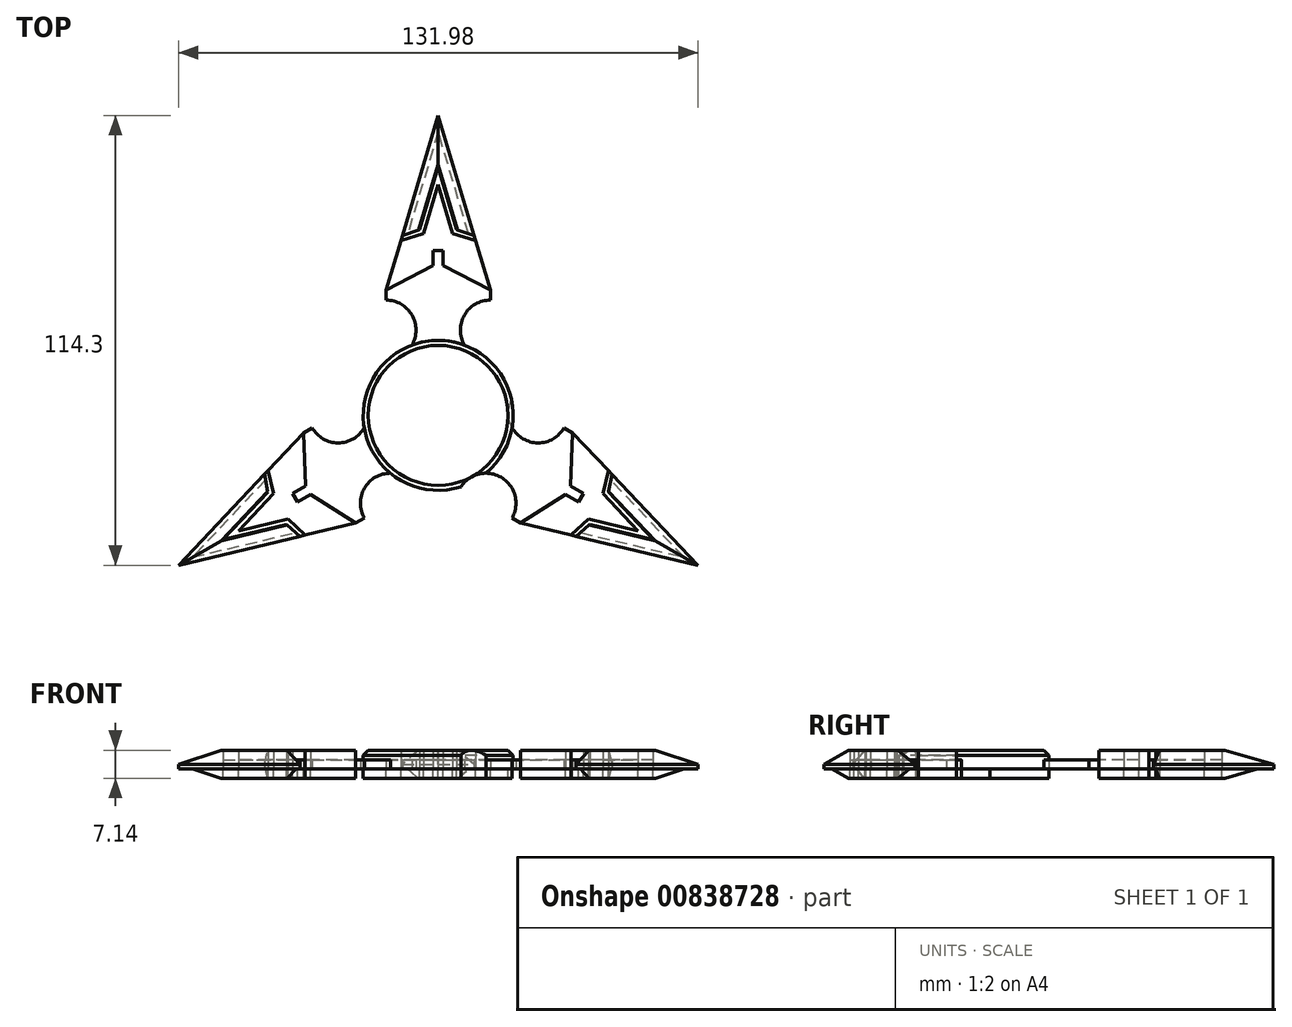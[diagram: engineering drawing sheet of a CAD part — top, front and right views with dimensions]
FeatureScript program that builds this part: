
annotation { "Feature Type Name" : "Feature", "Feature Type Description" : "" }
export const myFeature = defineFeature(function(context is Context, id is Id, definition is map)
    precondition{}
    {
        {
            var Q0;
            Q0=qCreatedBy(makeId("Top.planeOp"),FACE);
            var sketch = newSketch(context, id + "F0", { "sketchPlane" : qUnion([Q0])});
            skCircle(sketch, "E0", {"center": v(0, 0) * mm, "radius": 19.05 * mm});
            skLineSegment(sketch, "E1", {"start": v(0, 76.2) * mm, "end": v(-13.25, 31.83) * mm});
            skLineSegment(sketch, "E2", {"start": v(13.25, 31.83) * mm, "end": v(0, 76.2) * mm});
            skLineSegment(sketch, "E3", {"start": v(-13.25, 31.83) * mm, "end": v(-13.25, 29.3) * mm});
            skLineSegment(sketch, "E4", {"start": v(13.25, 31.83) * mm, "end": v(13.25, 29.3) * mm});
            skLineSegment(sketch, "E5", {"start": v(0, 0) * mm, "end": v(-4, 18.62) * mm});
            skPoint(sketch, "E6", {"position": v(-12.85, 14.06) * mm});
            skPoint(sketch, "E7", {"position": v(12.85, 14.06) * mm});
            skArc(sketch, "E8", {"start": v(-12.85, 14.06) * mm, "mid": v(-5.63, 21.87) * mm, "end": v(-13.25, 29.3) * mm});
            skArc(sketch, "E9", {"start": v(13.25, 29.3) * mm, "mid": v(5.63, 21.87) * mm, "end": v(12.85, 14.06) * mm});
            skPoint(sketch, "E10", {"position": v(0, 63.05) * mm});
            skPoint(sketch, "E11", {"position": v(-4.73, 47.22) * mm});
            skPoint(sketch, "E12", {"position": v(4.73, 47.22) * mm});
            skPoint(sketch, "E13", {"position": v(-9.1, 45.72) * mm});
            skPoint(sketch, "E14", {"position": v(9.12, 45.67) * mm});
            skLineSegment(sketch, "E15", {"start": v(-9.1, 45.72) * mm, "end": v(-4.73, 47.22) * mm});
            skLineSegment(sketch, "E16", {"start": v(0, 63.05) * mm, "end": v(-4.73, 47.22) * mm});
            skLineSegment(sketch, "E17", {"start": v(0, 63.05) * mm, "end": v(4.73, 47.22) * mm});
            skLineSegment(sketch, "E18", {"start": v(4.73, 47.22) * mm, "end": v(9.12, 45.67) * mm});
            skPoint(sketch, "E19", {"position": v(-9.48, 44.45) * mm});
            skPoint(sketch, "E20", {"position": v(9.48, 44.45) * mm});
            skPoint(sketch, "E21", {"position": v(0, 58.62) * mm});
            skLineSegment(sketch, "E22", {"start": v(-13.25, 31.83) * mm, "end": v(-1.27, 38.1) * mm});
            skLineSegment(sketch, "E23", {"start": v(-1.27, 38.1) * mm, "end": v(-1.27, 41.91) * mm});
            skLineSegment(sketch, "E24", {"start": v(-1.27, 41.91) * mm, "end": v(1.27, 41.91) * mm});
            skLineSegment(sketch, "E25", {"start": v(1.27, 41.91) * mm, "end": v(1.27, 38.1) * mm});
            skLineSegment(sketch, "E26", {"start": v(1.27, 38.1) * mm, "end": v(13.25, 31.83) * mm});
            skLineSegment(sketch, "E27", {"start": v(-9.48, 44.45) * mm, "end": v(-3.7, 46.2) * mm});
            skLineSegment(sketch, "E28", {"start": v(-3.7, 46.2) * mm, "end": v(0, 58.62) * mm});
            skLineSegment(sketch, "E29", {"start": v(0, 58.62) * mm, "end": v(3.7, 46.2) * mm});
            skLineSegment(sketch, "E30", {"start": v(3.7, 46.2) * mm, "end": v(9.48, 44.45) * mm});
            skPoint(sketch, "E31.1.0", {"position": v(-43.23, -14.01) * mm});
            skLineSegment(sketch, "E31.1.1", {"start": v(-66, -38.1) * mm, "end": v(-20.94, -27.39) * mm});
            skLineSegment(sketch, "E31.1.2", {"start": v(-33.63, -17.95) * mm, "end": v(-34.2, -4.44) * mm});
            skPoint(sketch, "E31.1.3", {"position": v(-54.6, -31.53) * mm});
            skLineSegment(sketch, "E31.1.4", {"start": v(-20.94, -27.39) * mm, "end": v(-32.36, -20.15) * mm});
            skLineSegment(sketch, "E31.1.5", {"start": v(-34.2, -4.44) * mm, "end": v(-66, -38.1) * mm});
            skPoint(sketch, "E31.1.6", {"position": v(-33.75, -30.44) * mm});
            skLineSegment(sketch, "E31.1.7", {"start": v(-54.6, -31.53) * mm, "end": v(-38.52, -27.7) * mm});
            skPoint(sketch, "E31.1.8", {"position": v(-38.52, -27.7) * mm});
            skLineSegment(sketch, "E31.1.9", {"start": v(-50.76, -29.3) * mm, "end": v(-41.86, -19.89) * mm});
            skPoint(sketch, "E31.1.10", {"position": v(-44.1, -14.94) * mm});
            skLineSegment(sketch, "E31.1.11", {"start": v(-54.6, -31.53) * mm, "end": v(-43.25, -19.51) * mm});
            skPoint(sketch, "E31.1.12", {"position": v(-50.76, -29.3) * mm});
            skPoint(sketch, "E31.1.13", {"position": v(-43.25, -19.51) * mm});
            skPoint(sketch, "E31.1.14", {"position": v(-35.04, -30.74) * mm});
            skLineSegment(sketch, "E31.1.15", {"start": v(-38.15, -26.3) * mm, "end": v(-50.76, -29.3) * mm});
            skLineSegment(sketch, "E31.1.16", {"start": v(-41.86, -19.89) * mm, "end": v(-43.23, -14.01) * mm});
            skLineSegment(sketch, "E31.1.17", {"start": v(-36.93, -19.86) * mm, "end": v(-33.63, -17.95) * mm});
            skLineSegment(sketch, "E31.1.18", {"start": v(-43.25, -19.51) * mm, "end": v(-44.1, -14.94) * mm});
            skLineSegment(sketch, "E31.1.19", {"start": v(-33.75, -30.44) * mm, "end": v(-38.15, -26.3) * mm});
            skLineSegment(sketch, "E31.1.20", {"start": v(-35.04, -30.74) * mm, "end": v(-38.52, -27.7) * mm});
            skLineSegment(sketch, "E31.1.21", {"start": v(-35.66, -22.05) * mm, "end": v(-36.93, -19.86) * mm});
            skLineSegment(sketch, "E31.1.22", {"start": v(-32.36, -20.15) * mm, "end": v(-35.66, -22.05) * mm});
            skLineSegment(sketch, "E31.1.23", {"start": v(-34.2, -4.44) * mm, "end": v(-32, -3.17) * mm});
            skLineSegment(sketch, "E31.1.24", {"start": v(-20.94, -27.39) * mm, "end": v(-18.74, -26.12) * mm});
            skArc(sketch, "E31.1.25", {"start": v(-32, -3.17) * mm, "mid": v(-21.75, -6.06) * mm, "end": v(-18.6, 4.1) * mm});
            skArc(sketch, "E31.1.26", {"start": v(-5.75, -18.16) * mm, "mid": v(-16.12, -15.81) * mm, "end": v(-18.74, -26.12) * mm});
            skPoint(sketch, "E31.2.0", {"position": v(33.75, -30.44) * mm});
            skLineSegment(sketch, "E31.2.1", {"start": v(66, -38.1) * mm, "end": v(34.2, -4.44) * mm});
            skLineSegment(sketch, "E31.2.2", {"start": v(32.36, -20.15) * mm, "end": v(20.94, -27.39) * mm});
            skPoint(sketch, "E31.2.3", {"position": v(54.6, -31.53) * mm});
            skLineSegment(sketch, "E31.2.4", {"start": v(34.2, -4.44) * mm, "end": v(33.63, -17.95) * mm});
            skLineSegment(sketch, "E31.2.5", {"start": v(20.94, -27.39) * mm, "end": v(66, -38.1) * mm});
            skPoint(sketch, "E31.2.6", {"position": v(43.23, -14.01) * mm});
            skLineSegment(sketch, "E31.2.7", {"start": v(54.6, -31.53) * mm, "end": v(43.25, -19.51) * mm});
            skPoint(sketch, "E31.2.8", {"position": v(43.25, -19.51) * mm});
            skLineSegment(sketch, "E31.2.9", {"start": v(50.76, -29.3) * mm, "end": v(38.15, -26.3) * mm});
            skPoint(sketch, "E31.2.10", {"position": v(35, -30.73) * mm});
            skLineSegment(sketch, "E31.2.11", {"start": v(54.6, -31.53) * mm, "end": v(38.52, -27.7) * mm});
            skPoint(sketch, "E31.2.12", {"position": v(50.76, -29.3) * mm});
            skPoint(sketch, "E31.2.13", {"position": v(38.52, -27.7) * mm});
            skPoint(sketch, "E31.2.14", {"position": v(44.15, -14.98) * mm});
            skLineSegment(sketch, "E31.2.15", {"start": v(41.86, -19.89) * mm, "end": v(50.76, -29.3) * mm});
            skLineSegment(sketch, "E31.2.16", {"start": v(38.15, -26.3) * mm, "end": v(33.75, -30.44) * mm});
            skLineSegment(sketch, "E31.2.17", {"start": v(35.66, -22.05) * mm, "end": v(32.36, -20.15) * mm});
            skLineSegment(sketch, "E31.2.18", {"start": v(38.52, -27.7) * mm, "end": v(35, -30.73) * mm});
            skLineSegment(sketch, "E31.2.19", {"start": v(43.23, -14.01) * mm, "end": v(41.86, -19.89) * mm});
            skLineSegment(sketch, "E31.2.20", {"start": v(44.15, -14.98) * mm, "end": v(43.25, -19.51) * mm});
            skLineSegment(sketch, "E31.2.21", {"start": v(36.93, -19.86) * mm, "end": v(35.66, -22.05) * mm});
            skLineSegment(sketch, "E31.2.22", {"start": v(33.63, -17.95) * mm, "end": v(36.93, -19.86) * mm});
            skLineSegment(sketch, "E31.2.23", {"start": v(20.94, -27.39) * mm, "end": v(18.74, -26.12) * mm});
            skLineSegment(sketch, "E31.2.24", {"start": v(34.2, -4.44) * mm, "end": v(32, -3.17) * mm});
            skArc(sketch, "E31.2.25", {"start": v(18.74, -26.12) * mm, "mid": v(16.12, -15.81) * mm, "end": v(5.75, -18.16) * mm});
            skArc(sketch, "E31.2.26", {"start": v(18.6, 4.1) * mm, "mid": v(21.75, -6.06) * mm, "end": v(32, -3.17) * mm});
            skArc(sketch, "E32", {"start": v(216.55, -0.25) * mm, "mid": v(245.18, 23.96) * mm, "end": v(209.9, 11.27) * mm});
            skLineSegment(sketch, "E33", {"start": v(228.68, 90.63) * mm, "end": v(219.2, 58.88) * mm});
            skLineSegment(sketch, "E34", {"start": v(241.93, 46.27) * mm, "end": v(228.68, 90.63) * mm});
            skLineSegment(sketch, "E35", {"start": v(241.93, 46.27) * mm, "end": v(241.93, 43.73) * mm});
            skPoint(sketch, "E36", {"position": v(215.83, 28.5) * mm});
            skPoint(sketch, "E37", {"position": v(241.53, 28.5) * mm});
            skArc(sketch, "E38", {"start": v(215.83, 28.5) * mm, "mid": v(223.05, 36.3) * mm, "end": v(215.43, 43.73) * mm});
            skArc(sketch, "E39", {"start": v(241.93, 43.73) * mm, "mid": v(234.3, 36.3) * mm, "end": v(241.53, 28.5) * mm});
            skPoint(sketch, "E40", {"position": v(228.68, 77.49) * mm});
            skPoint(sketch, "E41", {"position": v(223.95, 61.65) * mm});
            skPoint(sketch, "E42", {"position": v(233.4, 61.65) * mm});
            skPoint(sketch, "E43", {"position": v(219.58, 60.15) * mm});
            skPoint(sketch, "E44", {"position": v(237.8, 60.1) * mm});
            skLineSegment(sketch, "E45", {"start": v(219.58, 60.15) * mm, "end": v(223.95, 61.65) * mm});
            skLineSegment(sketch, "E46", {"start": v(228.68, 77.49) * mm, "end": v(223.95, 61.65) * mm});
            skLineSegment(sketch, "E47", {"start": v(228.68, 77.49) * mm, "end": v(233.4, 61.65) * mm});
            skLineSegment(sketch, "E48", {"start": v(233.4, 61.65) * mm, "end": v(237.8, 60.1) * mm});
            skPoint(sketch, "E49", {"position": v(219.2, 58.88) * mm});
            skPoint(sketch, "E50", {"position": v(238.16, 58.88) * mm});
            skPoint(sketch, "E51", {"position": v(228.68, 73.05) * mm});
            skLineSegment(sketch, "E52", {"start": v(215.43, 46.27) * mm, "end": v(227.4, 52.53) * mm});
            skLineSegment(sketch, "E53", {"start": v(227.4, 52.53) * mm, "end": v(227.4, 56.34) * mm});
            skLineSegment(sketch, "E54", {"start": v(227.4, 56.34) * mm, "end": v(229.95, 56.34) * mm});
            skLineSegment(sketch, "E55", {"start": v(229.95, 56.34) * mm, "end": v(229.95, 52.53) * mm});
            skLineSegment(sketch, "E56", {"start": v(229.95, 52.53) * mm, "end": v(241.93, 46.27) * mm});
            skLineSegment(sketch, "E57", {"start": v(219.2, 58.88) * mm, "end": v(224.97, 60.63) * mm});
            skLineSegment(sketch, "E58", {"start": v(224.97, 60.63) * mm, "end": v(228.68, 73.05) * mm});
            skLineSegment(sketch, "E59", {"start": v(228.68, 73.05) * mm, "end": v(232.39, 60.63) * mm});
            skLineSegment(sketch, "E60", {"start": v(232.39, 60.63) * mm, "end": v(238.16, 58.88) * mm});
            skPoint(sketch, "E61.1.0", {"position": v(185.44, 0.42) * mm});
            skLineSegment(sketch, "E61.1.1", {"start": v(193.63, -16.3) * mm, "end": v(194.92, -16) * mm});
            skLineSegment(sketch, "E61.1.2", {"start": v(195.05, -3.52) * mm, "end": v(194.49, 10) * mm});
            skPoint(sketch, "E61.1.3", {"position": v(174.07, -17.1) * mm});
            skLineSegment(sketch, "E61.1.4", {"start": v(207.73, -12.95) * mm, "end": v(196.32, -5.72) * mm});
            skLineSegment(sketch, "E61.1.5", {"start": v(194.49, 10) * mm, "end": v(185.44, 0.42) * mm});
            skPoint(sketch, "E61.1.6", {"position": v(194.92, -16) * mm});
            skPoint(sketch, "E61.1.8", {"position": v(190.15, -13.27) * mm});
            skPoint(sketch, "E61.1.10", {"position": v(184.57, -0.5) * mm});
            skPoint(sketch, "E61.1.12", {"position": v(177.92, -14.87) * mm});
            skPoint(sketch, "E61.1.13", {"position": v(185.42, -5.08) * mm});
            skPoint(sketch, "E61.1.14", {"position": v(193.63, -16.3) * mm});
            skLineSegment(sketch, "E61.1.17", {"start": v(191.75, -5.42) * mm, "end": v(195.05, -3.52) * mm});
            skLineSegment(sketch, "E61.1.21", {"start": v(193.02, -7.62) * mm, "end": v(191.75, -5.42) * mm});
            skLineSegment(sketch, "E61.1.22", {"start": v(196.32, -5.72) * mm, "end": v(193.02, -7.62) * mm});
            skLineSegment(sketch, "E61.1.23", {"start": v(194.49, 10) * mm, "end": v(196.69, 11.26) * mm});
            skLineSegment(sketch, "E61.1.24", {"start": v(207.73, -12.95) * mm, "end": v(209.93, -11.68) * mm});
            skArc(sketch, "E61.1.25", {"start": v(196.69, 11.26) * mm, "mid": v(206.92, 8.38) * mm, "end": v(210.07, 18.53) * mm});
            skArc(sketch, "E61.1.26", {"start": v(222.93, -3.73) * mm, "mid": v(212.55, -1.38) * mm, "end": v(209.93, -11.68) * mm});
            skPoint(sketch, "E61.2.0", {"position": v(262.43, -16) * mm});
            skLineSegment(sketch, "E61.2.1", {"start": v(294.67, -23.67) * mm, "end": v(262.87, 10) * mm});
            skLineSegment(sketch, "E61.2.2", {"start": v(261.04, -5.72) * mm, "end": v(249.62, -12.95) * mm});
            skPoint(sketch, "E61.2.3", {"position": v(283.28, -17.1) * mm});
            skLineSegment(sketch, "E61.2.4", {"start": v(262.87, 10) * mm, "end": v(262.3, -3.52) * mm});
            skLineSegment(sketch, "E61.2.5", {"start": v(249.62, -12.95) * mm, "end": v(294.67, -23.67) * mm});
            skPoint(sketch, "E61.2.6", {"position": v(271.91, 0.42) * mm});
            skLineSegment(sketch, "E61.2.7", {"start": v(283.28, -17.1) * mm, "end": v(271.93, -5.08) * mm});
            skPoint(sketch, "E61.2.8", {"position": v(271.93, -5.08) * mm});
            skLineSegment(sketch, "E61.2.9", {"start": v(279.44, -14.87) * mm, "end": v(266.83, -11.88) * mm});
            skPoint(sketch, "E61.2.10", {"position": v(263.67, -16.3) * mm});
            skLineSegment(sketch, "E61.2.11", {"start": v(283.28, -17.1) * mm, "end": v(267.2, -13.27) * mm});
            skPoint(sketch, "E61.2.12", {"position": v(279.44, -14.87) * mm});
            skPoint(sketch, "E61.2.13", {"position": v(267.2, -13.27) * mm});
            skPoint(sketch, "E61.2.14", {"position": v(272.82, -0.54) * mm});
            skLineSegment(sketch, "E61.2.15", {"start": v(270.54, -5.45) * mm, "end": v(279.44, -14.87) * mm});
            skLineSegment(sketch, "E61.2.16", {"start": v(266.83, -11.88) * mm, "end": v(262.43, -16) * mm});
            skLineSegment(sketch, "E61.2.17", {"start": v(264.34, -7.62) * mm, "end": v(261.04, -5.72) * mm});
            skLineSegment(sketch, "E61.2.18", {"start": v(267.2, -13.27) * mm, "end": v(263.67, -16.3) * mm});
            skLineSegment(sketch, "E61.2.19", {"start": v(271.91, 0.42) * mm, "end": v(270.54, -5.45) * mm});
            skLineSegment(sketch, "E61.2.20", {"start": v(272.82, -0.54) * mm, "end": v(271.93, -5.08) * mm});
            skLineSegment(sketch, "E61.2.21", {"start": v(265.6, -5.42) * mm, "end": v(264.34, -7.62) * mm});
            skLineSegment(sketch, "E61.2.22", {"start": v(262.3, -3.52) * mm, "end": v(265.6, -5.42) * mm});
            skLineSegment(sketch, "E61.2.23", {"start": v(249.62, -12.95) * mm, "end": v(247.42, -11.68) * mm});
            skLineSegment(sketch, "E61.2.24", {"start": v(262.87, 10) * mm, "end": v(260.67, 11.26) * mm});
            skArc(sketch, "E61.2.25", {"start": v(247.42, -11.68) * mm, "mid": v(244.8, -1.38) * mm, "end": v(234.43, -3.73) * mm});
            skArc(sketch, "E61.2.26", {"start": v(247.28, 18.53) * mm, "mid": v(250.43, 8.38) * mm, "end": v(260.67, 11.26) * mm});
            skPoint(sketch, "E62.orphan", {"position": v(162.69, -23.67) * mm});
            skPoint(sketch, "E63.orphan", {"position": v(215.43, 46.27) * mm});
            skSolve(sketch);
        }
        {
            var Q0;
            Q0=makeQuery(id+"F0.imprint","IMPRINT",FACE,{"disambiguationData":[TD([[makeQuery(id+"F0.imprint","IMPRINT",EDGE,{"derivedFrom":sQuery(id+"F0.wireOp",EDGE,"E31.2.2")}),-1.0]])]});
            var Q1;
            Q1=makeQuery(id+"F0.imprint","IMPRINT",FACE,{"disambiguationData":[TD([[makeQuery(id+"F0.imprint","IMPRINT",EDGE,{"derivedFrom":sQuery(id+"F0.wireOp",EDGE,"E31.1.2")}),-1.0]])]});
            var Q2;
            {var subQ5=sQuery(id+"F0.wireOp",EDGE,"E3");Q2=makeQuery(id+"F0.imprint","IMPRINT",FACE,{"disambiguationData":[TD([[makeQuery(id+"F0.imprint","IMPRINT",EDGE,{"derivedFrom":subQ5}),1.0]])]});}
            var Q3;
            {var subQ1=sQuery(id+"F0.wireOp",EDGE,"E15");Q3=makeQuery(id+"F0.imprint","IMPRINT",FACE,{"disambiguationData":[TD([[makeQuery(id+"F0.imprint","IMPRINT",EDGE,{"derivedFrom":subQ1}),-1.0]])]});}
            var Q4;
            Q4=makeQuery(id+"F0.imprint","IMPRINT",FACE,{"disambiguationData":[TD([[makeQuery(id+"F0.imprint","IMPRINT",EDGE,{"derivedFrom":sQuery(id+"F0.wireOp",EDGE,"E31.2.7")}),1.0]])]});
            var Q5;
            Q5=makeQuery(id+"F0.imprint","IMPRINT",FACE,{"disambiguationData":[TD([[makeQuery(id+"F0.imprint","IMPRINT",EDGE,{"derivedFrom":sQuery(id+"F0.wireOp",EDGE,"E31.1.7")}),1.0]])]});
            extrude(context, id + "F1", {"entities" : qUnion([Q0, Q1, Q2, Q3, Q4, Q5]), "depth" : 2.38 * mm, "offsetDistance" : 25.4 * mm});
        }
        {
            var Q0;
            {var subQ2=sQuery(id+"F0.wireOp",EDGE,"E22");Q0=makeQuery(id+"F0.imprint","IMPRINT",FACE,{"disambiguationData":[TD([[makeQuery(id+"F0.imprint","IMPRINT",EDGE,{"derivedFrom":subQ2}),1.0]])]});}
            var Q1;
            {var subQ0=sQuery(id+"F0.wireOp",EDGE,"E15");Q1=makeQuery(id+"F0.imprint","IMPRINT",FACE,{"disambiguationData":[TD([[makeQuery(id+"F0.imprint","IMPRINT",EDGE,{"derivedFrom":subQ0}),1.0]])]});}
            var Q2;
            {var subQ4=sQuery(id+"F0.wireOp",EDGE,"E31.2.2");Q2=makeQuery(id+"F0.imprint","IMPRINT",FACE,{"disambiguationData":[TD([[makeQuery(id+"F0.imprint","IMPRINT",EDGE,{"derivedFrom":subQ4}),1.0]])]});}
            var Q3;
            Q3=makeQuery(id+"F0.imprint","IMPRINT",FACE,{"disambiguationData":[TD([[makeQuery(id+"F0.imprint","IMPRINT",EDGE,{"derivedFrom":sQuery(id+"F0.wireOp",EDGE,"E31.2.7")}),-1.0]])]});
            var Q4;
            Q4=makeQuery(id+"F0.imprint","IMPRINT",FACE,{"disambiguationData":[TD([[makeQuery(id+"F0.imprint","IMPRINT",EDGE,{"derivedFrom":sQuery(id+"F0.wireOp",EDGE,"E31.1.7")}),-1.0]])]});
            var Q5;
            {var subQ4=sQuery(id+"F0.wireOp",EDGE,"E31.1.2");Q5=makeQuery(id+"F0.imprint","IMPRINT",FACE,{"disambiguationData":[TD([[makeQuery(id+"F0.imprint","IMPRINT",EDGE,{"derivedFrom":subQ4}),1.0]])]});}
            var Q6;
            Q6=makeQuery(id+"F0.imprint","IMPRINT",FACE,{"disambiguationData":[TD([[makeQuery(id+"F0.imprint","IMPRINT",EDGE,{"derivedFrom":sQuery(id+"F0.wireOp",EDGE,"HGt6zDVZ-n3Mf-MfAw-g2RU-08Ly1ao71fUC")}),-1.0]])]});
            var Q7;
            {var subQ0=sQuery(id+"F0.wireOp",EDGE,"E31.2.26");var subQ1=sQuery(id+"F0.wireOp",EDGE,"E0");var subQ2=makeQuery(id+"F0.imprint","INTERSECT",VERTEX,{"disambiguationData":[OD(0.0)],"derivedFrom":[subQ1,subQ0]});Q7=makeQuery(id+"F0.imprint","IMPRINT",FACE,{"disambiguationData":[TD([[makeQuery(id+"F0.imprint","IMPRINT",EDGE,{"disambiguationData":[TD([[subQ2,1.0]])],"derivedFrom":subQ1}),1.0]])]});}
            var Q8;
            {var subQ0=sQuery(id+"F0.wireOp",EDGE,"E31.2.25");var subQ1=sQuery(id+"F0.wireOp",EDGE,"E0");var subQ2=makeQuery(id+"F0.imprint","INTERSECT",VERTEX,{"disambiguationData":[OD(0.0)],"derivedFrom":[subQ1,subQ0]});Q8=makeQuery(id+"F0.imprint","IMPRINT",FACE,{"disambiguationData":[TD([[makeQuery(id+"F0.imprint","IMPRINT",EDGE,{"disambiguationData":[TD([[subQ2,-1.0]])],"derivedFrom":subQ1}),1.0]])]});}
            var Q9;
            {var subQ0=sQuery(id+"F0.wireOp",EDGE,"E31.1.26");var subQ1=sQuery(id+"F0.wireOp",EDGE,"E0");var subQ2=makeQuery(id+"F0.imprint","INTERSECT",VERTEX,{"disambiguationData":[OD(0.0)],"derivedFrom":[subQ1,subQ0]});Q9=makeQuery(id+"F0.imprint","IMPRINT",FACE,{"disambiguationData":[TD([[makeQuery(id+"F0.imprint","IMPRINT",EDGE,{"disambiguationData":[TD([[subQ2,1.0]])],"derivedFrom":subQ1}),1.0]])]});}
            var Q10;
            {var subQ0=sQuery(id+"F0.wireOp",EDGE,"E31.1.25");var subQ1=sQuery(id+"F0.wireOp",EDGE,"E0");var subQ2=makeQuery(id+"F0.imprint","INTERSECT",VERTEX,{"disambiguationData":[OD(0.0)],"derivedFrom":[subQ1,subQ0]});Q10=makeQuery(id+"F0.imprint","IMPRINT",FACE,{"disambiguationData":[TD([[makeQuery(id+"F0.imprint","IMPRINT",EDGE,{"disambiguationData":[TD([[subQ2,-1.0]])],"derivedFrom":subQ1}),1.0]])]});}
            var Q11;
            {var subQ0=sQuery(id+"F0.wireOp",EDGE,"E8");var subQ1=sQuery(id+"F0.wireOp",EDGE,"E0");var subQ2=makeQuery(id+"F0.imprint","INTERSECT",VERTEX,{"disambiguationData":[OD(0.0)],"derivedFrom":[subQ1,subQ0]});Q11=makeQuery(id+"F0.imprint","IMPRINT",FACE,{"disambiguationData":[TD([[makeQuery(id+"F0.imprint","IMPRINT",EDGE,{"disambiguationData":[TD([[subQ2,1.0]])],"derivedFrom":subQ1}),1.0]])]});}
            var Q12;
            {var subQ0=sQuery(id+"F0.wireOp",EDGE,"E9");var subQ1=sQuery(id+"F0.wireOp",EDGE,"E0");var subQ2=makeQuery(id+"F0.imprint","INTERSECT",VERTEX,{"disambiguationData":[OD(0.0)],"derivedFrom":[subQ1,subQ0]});Q12=makeQuery(id+"F0.imprint","IMPRINT",FACE,{"disambiguationData":[TD([[makeQuery(id+"F0.imprint","IMPRINT",EDGE,{"disambiguationData":[TD([[subQ2,-1.0]])],"derivedFrom":subQ1}),1.0]])]});}
            extrude(context, id + "F2", {"entities" : qUnion([Q0, Q1, Q2, Q3, Q4, Q5, Q6, Q7, Q8, Q9, Q10, Q11, Q12]), "depth" : 4.76 * mm, "offsetDistance" : 25.4 * mm});
        }
        {
            var Q0;
            Q0=makeQuery(id+"F0.imprint","IMPRINT",FACE,{"disambiguationData":[TD([[makeQuery(id+"F0.imprint","IMPRINT",EDGE,{"derivedFrom":sQuery(id+"F0.wireOp",EDGE,"HGt6zDVZ-n3Mf-MfAw-g2RU-08Ly1ao71fUC")}),-1.0]])]});
            var Q1;
            {var subQ0=sQuery(id+"F0.wireOp",EDGE,"E31.2.25");var subQ1=sQuery(id+"F0.wireOp",EDGE,"E0");var subQ2=makeQuery(id+"F0.imprint","INTERSECT",VERTEX,{"disambiguationData":[OD(0.0)],"derivedFrom":[subQ1,subQ0]});Q1=makeQuery(id+"F0.imprint","IMPRINT",FACE,{"disambiguationData":[TD([[makeQuery(id+"F0.imprint","IMPRINT",EDGE,{"disambiguationData":[TD([[subQ2,-1.0]])],"derivedFrom":subQ1}),1.0]])]});}
            var Q2;
            {var subQ0=sQuery(id+"F0.wireOp",EDGE,"E31.1.26");var subQ1=sQuery(id+"F0.wireOp",EDGE,"E0");var subQ2=makeQuery(id+"F0.imprint","INTERSECT",VERTEX,{"disambiguationData":[OD(0.0)],"derivedFrom":[subQ1,subQ0]});Q2=makeQuery(id+"F0.imprint","IMPRINT",FACE,{"disambiguationData":[TD([[makeQuery(id+"F0.imprint","IMPRINT",EDGE,{"disambiguationData":[TD([[subQ2,1.0]])],"derivedFrom":subQ1}),1.0]])]});}
            var Q3;
            {var subQ0=sQuery(id+"F0.wireOp",EDGE,"E31.1.25");var subQ1=sQuery(id+"F0.wireOp",EDGE,"E0");var subQ2=makeQuery(id+"F0.imprint","INTERSECT",VERTEX,{"disambiguationData":[OD(0.0)],"derivedFrom":[subQ1,subQ0]});Q3=makeQuery(id+"F0.imprint","IMPRINT",FACE,{"disambiguationData":[TD([[makeQuery(id+"F0.imprint","IMPRINT",EDGE,{"disambiguationData":[TD([[subQ2,-1.0]])],"derivedFrom":subQ1}),1.0]])]});}
            var Q4;
            {var subQ0=sQuery(id+"F0.wireOp",EDGE,"E8");var subQ1=sQuery(id+"F0.wireOp",EDGE,"E0");var subQ2=makeQuery(id+"F0.imprint","INTERSECT",VERTEX,{"disambiguationData":[OD(0.0)],"derivedFrom":[subQ1,subQ0]});Q4=makeQuery(id+"F0.imprint","IMPRINT",FACE,{"disambiguationData":[TD([[makeQuery(id+"F0.imprint","IMPRINT",EDGE,{"disambiguationData":[TD([[subQ2,1.0]])],"derivedFrom":subQ1}),1.0]])]});}
            var Q5;
            {var subQ0=sQuery(id+"F0.wireOp",EDGE,"E9");var subQ1=sQuery(id+"F0.wireOp",EDGE,"E0");var subQ2=makeQuery(id+"F0.imprint","INTERSECT",VERTEX,{"disambiguationData":[OD(0.0)],"derivedFrom":[subQ1,subQ0]});Q5=makeQuery(id+"F0.imprint","IMPRINT",FACE,{"disambiguationData":[TD([[makeQuery(id+"F0.imprint","IMPRINT",EDGE,{"disambiguationData":[TD([[subQ2,-1.0]])],"derivedFrom":subQ1}),1.0]])]});}
            var Q6;
            {var subQ4=sQuery(id+"F0.wireOp",EDGE,"E31.2.2");Q6=makeQuery(id+"F0.imprint","IMPRINT",FACE,{"disambiguationData":[TD([[makeQuery(id+"F0.imprint","IMPRINT",EDGE,{"derivedFrom":subQ4}),1.0]])]});}
            var Q7;
            Q7=makeQuery(id+"F0.imprint","IMPRINT",FACE,{"disambiguationData":[TD([[makeQuery(id+"F0.imprint","IMPRINT",EDGE,{"derivedFrom":sQuery(id+"F0.wireOp",EDGE,"E31.2.7")}),-1.0]])]});
            var Q8;
            {var subQ4=sQuery(id+"F0.wireOp",EDGE,"E31.1.2");Q8=makeQuery(id+"F0.imprint","IMPRINT",FACE,{"disambiguationData":[TD([[makeQuery(id+"F0.imprint","IMPRINT",EDGE,{"derivedFrom":subQ4}),1.0]])]});}
            var Q9;
            Q9=makeQuery(id+"F0.imprint","IMPRINT",FACE,{"disambiguationData":[TD([[makeQuery(id+"F0.imprint","IMPRINT",EDGE,{"derivedFrom":sQuery(id+"F0.wireOp",EDGE,"E31.1.7")}),-1.0]])]});
            var Q10;
            {var subQ2=sQuery(id+"F0.wireOp",EDGE,"E22");Q10=makeQuery(id+"F0.imprint","IMPRINT",FACE,{"disambiguationData":[TD([[makeQuery(id+"F0.imprint","IMPRINT",EDGE,{"derivedFrom":subQ2}),1.0]])]});}
            var Q11;
            {var subQ0=sQuery(id+"F0.wireOp",EDGE,"E15");Q11=makeQuery(id+"F0.imprint","IMPRINT",FACE,{"disambiguationData":[TD([[makeQuery(id+"F0.imprint","IMPRINT",EDGE,{"derivedFrom":subQ0}),1.0]])]});}
            extrude(context, id + "F3", {"entities" : qUnion([Q0, Q1, Q2, Q3, Q4, Q5, Q6, Q7, Q8, Q9, Q10, Q11]), "oppositeDirection" : true, "depth" : 2.38 * mm, "offsetDistance" : 25.4 * mm});
        }
        {
            var Q0;
            {var subQ0=sQuery(id+"F0.wireOp",EDGE,"E31.1.1");Q0=makeQuery(id+"F2.opExtrude","CAP_EDGE",EDGE,{"disambiguationData":[OSD([subQ0]),TDD([makeQuery(id+"F0.imprint","IMPRINT",EDGE,{"disambiguationData":[TD([[makeQuery(id+"F0.imprint","INTERSECT",VERTEX,{"derivedFrom":[subQ0,sQuery(id+"F0.wireOp",EDGE,"E31.1.5")]}),-1.0]])],"derivedFrom":subQ0})])],"isStart":false});}
            var Q1;
            {var subQ0=sQuery(id+"F0.wireOp",EDGE,"E31.1.1");Q1=makeQuery(id+"F3.opExtrude","CAP_EDGE",EDGE,{"disambiguationData":[OSD([subQ0]),TDD([makeQuery(id+"F0.imprint","IMPRINT",EDGE,{"disambiguationData":[TD([[makeQuery(id+"F0.imprint","INTERSECT",VERTEX,{"derivedFrom":[subQ0,sQuery(id+"F0.wireOp",EDGE,"E31.1.5")]}),-1.0]])],"derivedFrom":subQ0})])],"isStart":false});}
            var Q2;
            {var subQ0=sQuery(id+"F0.wireOp",EDGE,"E31.1.5");Q2=makeQuery(id+"F2.opExtrude","CAP_EDGE",EDGE,{"disambiguationData":[OSD([subQ0]),TDD([makeQuery(id+"F0.imprint","IMPRINT",EDGE,{"disambiguationData":[TD([[makeQuery(id+"F0.imprint","INTERSECT",VERTEX,{"derivedFrom":[sQuery(id+"F0.wireOp",EDGE,"E31.1.1"),subQ0]}),1.0]])],"derivedFrom":subQ0})])],"isStart":false});}
            var Q3;
            {var subQ0=sQuery(id+"F0.wireOp",EDGE,"E31.1.5");Q3=makeQuery(id+"F3.opExtrude","CAP_EDGE",EDGE,{"disambiguationData":[OSD([subQ0]),TDD([makeQuery(id+"F0.imprint","IMPRINT",EDGE,{"disambiguationData":[TD([[makeQuery(id+"F0.imprint","INTERSECT",VERTEX,{"derivedFrom":[sQuery(id+"F0.wireOp",EDGE,"E31.1.1"),subQ0]}),1.0]])],"derivedFrom":subQ0})])],"isStart":false});}
            var Q4;
            {var subQ0=sQuery(id+"F0.wireOp",EDGE,"E31.2.5");Q4=makeQuery(id+"F2.opExtrude","CAP_EDGE",EDGE,{"disambiguationData":[OSD([subQ0]),TDD([makeQuery(id+"F0.imprint","IMPRINT",EDGE,{"disambiguationData":[TD([[makeQuery(id+"F0.imprint","INTERSECT",VERTEX,{"derivedFrom":[sQuery(id+"F0.wireOp",EDGE,"E31.2.1"),subQ0]}),1.0]])],"derivedFrom":subQ0})])],"isStart":false});}
            var Q5;
            {var subQ0=sQuery(id+"F0.wireOp",EDGE,"E31.2.5");Q5=makeQuery(id+"F3.opExtrude","CAP_EDGE",EDGE,{"disambiguationData":[OSD([subQ0]),TDD([makeQuery(id+"F0.imprint","IMPRINT",EDGE,{"disambiguationData":[TD([[makeQuery(id+"F0.imprint","INTERSECT",VERTEX,{"derivedFrom":[sQuery(id+"F0.wireOp",EDGE,"E31.2.1"),subQ0]}),1.0]])],"derivedFrom":subQ0})])],"isStart":false});}
            var Q6;
            {var subQ0=sQuery(id+"F0.wireOp",EDGE,"E31.2.1");Q6=makeQuery(id+"F2.opExtrude","CAP_EDGE",EDGE,{"disambiguationData":[OSD([subQ0]),TDD([makeQuery(id+"F0.imprint","IMPRINT",EDGE,{"disambiguationData":[TD([[makeQuery(id+"F0.imprint","INTERSECT",VERTEX,{"derivedFrom":[subQ0,sQuery(id+"F0.wireOp",EDGE,"E31.2.5")]}),-1.0]])],"derivedFrom":subQ0})])],"isStart":false});}
            var Q7;
            {var subQ0=sQuery(id+"F0.wireOp",EDGE,"E31.2.1");Q7=makeQuery(id+"F3.opExtrude","CAP_EDGE",EDGE,{"disambiguationData":[OSD([subQ0]),TDD([makeQuery(id+"F0.imprint","IMPRINT",EDGE,{"disambiguationData":[TD([[makeQuery(id+"F0.imprint","INTERSECT",VERTEX,{"derivedFrom":[subQ0,sQuery(id+"F0.wireOp",EDGE,"E31.2.5")]}),-1.0]])],"derivedFrom":subQ0})])],"isStart":false});}
            var Q8;
            {var subQ0=sQuery(id+"F0.wireOp",EDGE,"E2");Q8=makeQuery(id+"F2.opExtrude","CAP_EDGE",EDGE,{"disambiguationData":[OSD([subQ0]),TDD([makeQuery(id+"F0.imprint","IMPRINT",EDGE,{"disambiguationData":[TD([[makeQuery(id+"F0.imprint","INTERSECT",VERTEX,{"derivedFrom":[sQuery(id+"F0.wireOp",EDGE,"E1"),subQ0]}),1.0]])],"derivedFrom":subQ0})])],"isStart":false});}
            var Q9;
            {var subQ0=sQuery(id+"F0.wireOp",EDGE,"E2");Q9=makeQuery(id+"F3.opExtrude","CAP_EDGE",EDGE,{"disambiguationData":[OSD([subQ0]),TDD([makeQuery(id+"F0.imprint","IMPRINT",EDGE,{"disambiguationData":[TD([[makeQuery(id+"F0.imprint","INTERSECT",VERTEX,{"derivedFrom":[sQuery(id+"F0.wireOp",EDGE,"E1"),subQ0]}),1.0]])],"derivedFrom":subQ0})])],"isStart":false});}
            var Q10;
            {var subQ0=sQuery(id+"F0.wireOp",EDGE,"E1");Q10=makeQuery(id+"F3.opExtrude","CAP_EDGE",EDGE,{"disambiguationData":[OSD([subQ0]),TDD([makeQuery(id+"F0.imprint","IMPRINT",EDGE,{"disambiguationData":[TD([[makeQuery(id+"F0.imprint","INTERSECT",VERTEX,{"derivedFrom":[subQ0,sQuery(id+"F0.wireOp",EDGE,"E2")]}),-1.0]])],"derivedFrom":subQ0})])],"isStart":false});}
            var Q11;
            {var subQ0=sQuery(id+"F0.wireOp",EDGE,"E1");Q11=makeQuery(id+"F2.opExtrude","CAP_EDGE",EDGE,{"disambiguationData":[OSD([subQ0]),TDD([makeQuery(id+"F0.imprint","IMPRINT",EDGE,{"disambiguationData":[TD([[makeQuery(id+"F0.imprint","INTERSECT",VERTEX,{"derivedFrom":[subQ0,sQuery(id+"F0.wireOp",EDGE,"E2")]}),-1.0]])],"derivedFrom":subQ0})])],"isStart":false});}
            chamfer(context, id + "F4", {"entities" : qUnion([Q0, Q1, Q2, Q3, Q4, Q5, Q6, Q7, Q8, Q9, Q10, Q11]), "width" : 3.57 * mm, "tangentPropagation" : true});
        }
        {
            var Q0;
            Q0=makeQuery(id+"F2.opExtrude","CAP_EDGE",EDGE,{"disambiguationData":[OSD([sQuery(id+"F0.wireOp",EDGE,"E0")])],"isStart":false});
            var Q1;
            Q1=makeQuery(id+"F2.opExtrude","CAP_EDGE",EDGE,{"disambiguationData":[OSD([sQuery(id+"F0.wireOp",EDGE,"HGt6zDVZ-n3Mf-MfAw-g2RU-08Ly1ao71fUC")])],"isStart":false});
            chamfer(context, id + "F5", {"entities" : qUnion([Q0, Q1]), "width" : 1.27 * mm, "tangentPropagation" : true});
        }
    });
